# Revit family: Kimberley Clark Professional Touchless Electronic Skincare Dispenser 92147 Family
name_source: partatom
category: Generic Models
revit_build: Autodesk Revit 2018 (Build: 20180329_1100(x64)
units: mm (PartAtom-declared; Revit-internal decimal feet)

## family parameters
Always vertical = Yes
Can host rebar = No
Cut with Voids When Loaded = No
Host = Wall
Part Type = Normal
Room Calculation Point = No
Round Connector Dimension = Use Diameter
Shared = No

## types (1)
- Kimberley Clark Professional Touchless Electronic Skincare Dispenser
    Distance From Floor = 1400 mm  [stored 4.59318 ft]
    Length = 287 mm
    Manufacturer = Kimberly Clark
    Material = Snow
    Model = Kimberley Clark Professional Touchless Electronic Skincare Dispenser 92147
    Telephone = 011 456 5911
    Thickness = 102 mm
    URL = www.kcprofessional.co.za
    Width = 184 mm

note: [stored X ft] marks values corroborated as IEEE doubles in the binary element streams (Revit-internal decimal feet)

## geometry (parser evidence)
native form markers: Sweep x3
no freeform markers — native parametric forms only
